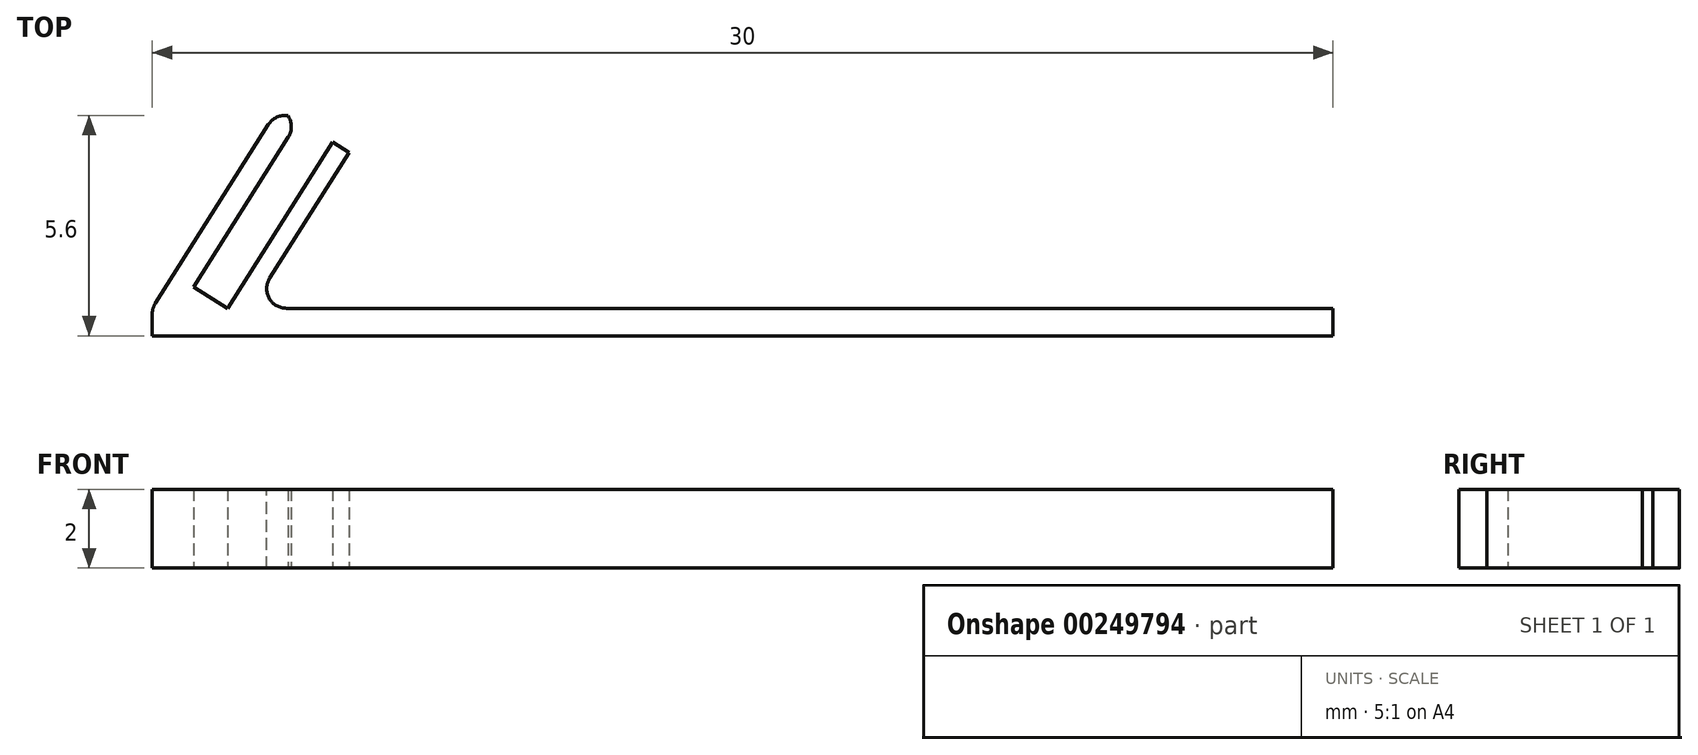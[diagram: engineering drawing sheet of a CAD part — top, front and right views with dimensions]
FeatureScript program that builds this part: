
annotation { "Feature Type Name" : "Feature", "Feature Type Description" : "" }
export const myFeature = defineFeature(function(context is Context, id is Id, definition is map)
    precondition{}
    {
        {
            var Q0;
            Q0=qCreatedBy(makeId("Top.planeOp"),FACE);
            var sketch = newSketch(context, id + "F0", { "sketchPlane" : qUnion([Q0])});
            skLineSegment(sketch, "E0.bottom", {"start": v(0, 0) * mm, "end": v(30, 0) * mm});
            skLineSegment(sketch, "E0.left", {"start": v(0, 0) * mm, "end": v(0, 0.7) * mm});
            skLineSegment(sketch, "E0.right", {"start": v(30, 0) * mm, "end": v(30, 0.7) * mm});
            skLineSegment(sketch, "E1", {"start": v(0, 0.7) * mm, "end": v(3.21, 5.79) * mm});
            skLineSegment(sketch, "E2", {"start": v(3.21, 5.79) * mm, "end": v(3.72, 5.47) * mm});
            skLineSegment(sketch, "E3", {"start": v(3.72, 5.47) * mm, "end": v(1.05, 1.24) * mm});
            skLineSegment(sketch, "E4", {"start": v(1.9, 0.7) * mm, "end": v(4.58, 4.93) * mm});
            skLineSegment(sketch, "E5", {"start": v(4.58, 4.93) * mm, "end": v(5, 4.66) * mm});
            skLineSegment(sketch, "E6", {"start": v(5, 4.66) * mm, "end": v(2.5, 0.7) * mm});
            skLineSegment(sketch, "E7", {"start": v(1.9, 0.7) * mm, "end": v(1.05, 1.24) * mm});
            skLineSegment(sketch, "E8.trimOffspring", {"start": v(2.5, 0.7) * mm, "end": v(30, 0.7) * mm});
            skSolve(sketch);
        }
        {
            var Q0;
            Q0=makeQuery(id+"F0.imprint","IMPRINT",FACE,{"disambiguationData":[TD([[makeQuery(id+"F0.imprint","IMPRINT",EDGE,{"derivedFrom":sQuery(id+"F0.wireOp",EDGE,"E0.bottom")}),1.0]])]});
            extrude(context, id + "F1", {"entities" : qUnion([Q0]), "depth" : 2 * mm});
        }
        {
            var Q0;
            Q0=makeQuery(id+"F1.opExtrude","SWEPT_EDGE",EDGE,{"disambiguationData":[OSD([sQuery(id+"F0.wireOp",EDGE,"E0.left"),sQuery(id+"F0.wireOp",EDGE,"E1")])]});
            var Q1;
            Q1=makeQuery(id+"F1.opExtrude","SWEPT_EDGE",EDGE,{"disambiguationData":[OSD([sQuery(id+"F0.wireOp",EDGE,"E6"),sQuery(id+"F0.wireOp",EDGE,"E8.trimOffspring")])]});
            var Q2;
            Q2=makeQuery(id+"F1.opExtrude","SWEPT_EDGE",EDGE,{"disambiguationData":[OSD([sQuery(id+"F0.wireOp",EDGE,"E1"),sQuery(id+"F0.wireOp",EDGE,"E2")])]});
            var Q3;
            Q3=makeQuery(id+"F1.opExtrude","SWEPT_EDGE",EDGE,{"disambiguationData":[OSD([sQuery(id+"F0.wireOp",EDGE,"E2"),sQuery(id+"F0.wireOp",EDGE,"E3")])]});
            fillet(context, id + "F2", {"entities" : qUnion([Q0, Q1, Q2, Q3]), "radius" : 0.5 * mm, "tangentPropagation" : true, "allowEdgeOverflow" : false});
        }
    });
